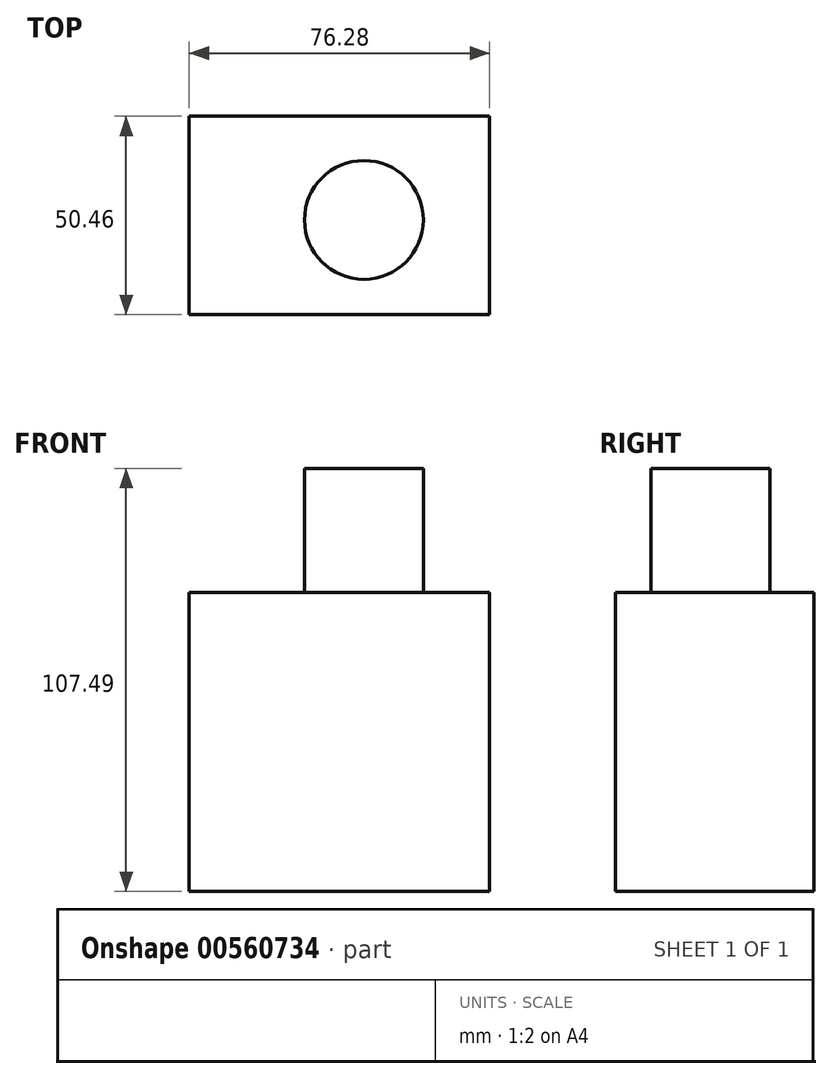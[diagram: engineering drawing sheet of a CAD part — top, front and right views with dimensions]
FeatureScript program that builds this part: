
annotation { "Feature Type Name" : "Feature", "Feature Type Description" : "" }
export const myFeature = defineFeature(function(context is Context, id is Id, definition is map)
    precondition{}
    {
        {
            var Q0;
            Q0=qCreatedBy(makeId("Front.planeOp"),FACE);
            var sketch = newSketch(context, id + "F0", { "sketchPlane" : qUnion([Q0])});
            skLineSegment(sketch, "E0.bottom", {"start": v(-76.28, -75.92) * mm, "end": v(0, -75.92) * mm});
            skLineSegment(sketch, "E0.top", {"start": v(-76.28, 0) * mm, "end": v(0, 0) * mm});
            skLineSegment(sketch, "E0.left", {"start": v(-76.28, -75.92) * mm, "end": v(-76.28, 0) * mm});
            skLineSegment(sketch, "E0.right", {"start": v(0, -75.92) * mm, "end": v(0, 0) * mm});
            skSolve(sketch);
        }
        {
            var Q0;
            Q0=makeQuery(id+"F0.imprint","IMPRINT",FACE,{"disambiguationData":[TD([[makeQuery(id+"F0.imprint","IMPRINT",EDGE,{"derivedFrom":sQuery(id+"F0.wireOp",EDGE,"E0.bottom")}),1.0]])]});
            extrude(context, id + "F1", {"entities" : qUnion([Q0]), "depth" : 50.46 * mm, "offsetDistance" : 25.4 * mm});
        }
        {
            var Q0;
            Q0=makeQuery(id+"F1.opExtrude","SWEPT_FACE",FACE,{"disambiguationData":[OSD([sQuery(id+"F0.wireOp",EDGE,"E0.top")])]});
            var sketch = newSketch(context, id + "F2", { "sketchPlane" : qUnion([Q0])});
            skCircle(sketch, "E1", {"center": v(-31.9, -26.37) * mm, "radius": 15.1 * mm});
            skSolve(sketch);
        }
        {
            var Q0;
            Q0=makeQuery(id+"F2.imprint","IMPRINT",FACE,{"disambiguationData":[TD([[makeQuery(id+"F2.imprint","IMPRINT",EDGE,{"derivedFrom":sQuery(id+"F2.wireOp",EDGE,"E1")}),1.0]])]});
            extrude(context, id + "F3", {"entities" : qUnion([Q0]), "operationType" : NewBodyOperationType.ADD, "depth" : 31.57 * mm, "offsetDistance" : 25.4 * mm});
        }
    });
